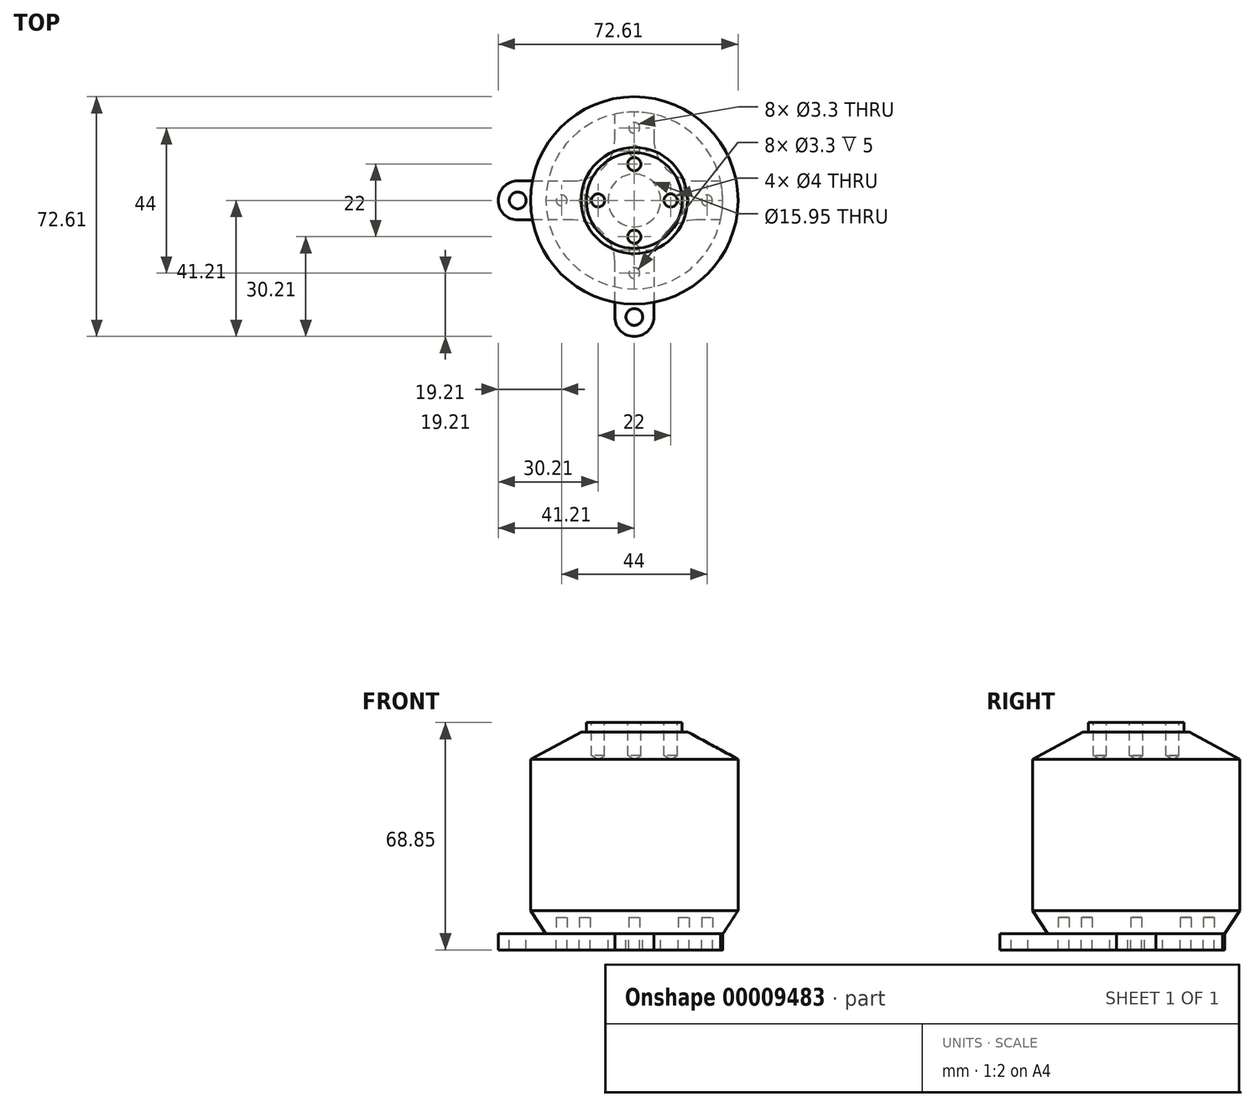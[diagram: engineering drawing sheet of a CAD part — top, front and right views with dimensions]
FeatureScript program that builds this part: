
annotation { "Feature Type Name" : "Feature", "Feature Type Description" : "" }
export const myFeature = defineFeature(function(context is Context, id is Id, definition is map)
    precondition{}
    {
        {
            var Q0;
            Q0=qCreatedBy(makeId("Front.planeOp"),FACE);
            var sketch = newSketch(context, id + "F0", { "sketchPlane" : qUnion([Q0])});
            skLineSegment(sketch, "E0", {"start": v(0, 0) * mm, "end": v(26.8, 0) * mm});
            skLineSegment(sketch, "E1", {"start": v(31.4, 7.03) * mm, "end": v(31.4, 52.91) * mm});
            skLineSegment(sketch, "E2", {"start": v(14.5, 64) * mm, "end": v(0, 64) * mm});
            skLineSegment(sketch, "E3", {"start": v(0, 64) * mm, "end": v(0, 0) * mm});
            skLineSegment(sketch, "E4.bottom", {"start": v(0, 0) * mm, "end": v(5, 0) * mm});
            skLineSegment(sketch, "E4.top", {"start": v(0, -24) * mm, "end": v(5, -24) * mm});
            skLineSegment(sketch, "E4.left", {"start": v(0, 0) * mm, "end": v(0, -24) * mm});
            skLineSegment(sketch, "E4.right", {"start": v(5, 0) * mm, "end": v(5, -24) * mm});
            skLineSegment(sketch, "E5", {"start": v(14.5, 64) * mm, "end": v(14.5, 61.2) * mm});
            skLineSegment(sketch, "E6", {"start": v(14.5, 61.2) * mm, "end": v(16.1, 61.2) * mm});
            skLineSegment(sketch, "E7", {"start": v(16.1, 61.2) * mm, "end": v(31.4, 52.91) * mm});
            skLineSegment(sketch, "E8", {"start": v(31.4, 7.03) * mm, "end": v(26.8, 0) * mm});
            skSolve(sketch);
        }
        {
            var Q0;
            Q0=makeQuery(id+"F0.imprint","IMPRINT",FACE,{"disambiguationData":[TD([[makeQuery(id+"F0.imprint","IMPRINT",EDGE,{"derivedFrom":sQuery(id+"F0.wireOp",EDGE,"E0")}),1.0]])]});
            var Q1;
            Q1=makeQuery(id+"F0.imprint","IMPRINT",FACE,{"disambiguationData":[TD([[makeQuery(id+"F0.imprint","IMPRINT",EDGE,{"derivedFrom":sQuery(id+"F0.wireOp",EDGE,"E4.bottom")}),-1.0]])]});
            var Q2;
            Q2=sQuery(id+"F0.wireOp",EDGE,"E3");
            revolve(context, id + "F1", {"entities" : qUnion([Q0, Q1]), "axis" : qUnion([Q2]), "revolveType" : RevolveType.FULL});
        }
        {
            var Q0;
            Q0=makeQuery(id+"F1.opRevolve","SWEPT_FACE",FACE,{"disambiguationData":[OSD([sQuery(id+"F0.wireOp",EDGE,"E0")])]});
            var sketch = newSketch(context, id + "F2", { "sketchPlane" : qUnion([Q0])});
            skCircle(sketch, "E9", {"center": v(-22, 0) * mm, "radius": 1.65 * mm});
            skCircle(sketch, "E10", {"center": v(-15, 0) * mm, "radius": 1.65 * mm});
            skCircle(sketch, "E11.1.0", {"center": v(0, -22) * mm, "radius": 1.65 * mm});
            skCircle(sketch, "E11.1.1", {"center": v(0, -15) * mm, "radius": 1.65 * mm});
            skCircle(sketch, "E11.2.0", {"center": v(22, 0) * mm, "radius": 1.65 * mm});
            skCircle(sketch, "E11.2.1", {"center": v(15, 0) * mm, "radius": 1.65 * mm});
            skCircle(sketch, "E11.3.0", {"center": v(0, 22) * mm, "radius": 1.65 * mm});
            skCircle(sketch, "E11.3.1", {"center": v(0, 15) * mm, "radius": 1.65 * mm});
            skPoint(sketch, "E11.center", {"position": v(0, 0) * mm});
            skSolve(sketch);
        }
        {
            var Q0;
            Q0=makeQuery(id+"F2.imprint","IMPRINT",FACE,{"disambiguationData":[TD([[makeQuery(id+"F2.imprint","IMPRINT",EDGE,{"derivedFrom":sQuery(id+"F2.wireOp",EDGE,"E9")}),1.0]])]});
            var Q1;
            Q1=makeQuery(id+"F2.imprint","IMPRINT",FACE,{"disambiguationData":[TD([[makeQuery(id+"F2.imprint","IMPRINT",EDGE,{"derivedFrom":sQuery(id+"F2.wireOp",EDGE,"E10")}),1.0]])]});
            var Q2;
            Q2=makeQuery(id+"F2.imprint","IMPRINT",FACE,{"disambiguationData":[TD([[makeQuery(id+"F2.imprint","IMPRINT",EDGE,{"derivedFrom":sQuery(id+"F2.wireOp",EDGE,"E11.3.1")}),1.0]])]});
            var Q3;
            Q3=makeQuery(id+"F2.imprint","IMPRINT",FACE,{"disambiguationData":[TD([[makeQuery(id+"F2.imprint","IMPRINT",EDGE,{"derivedFrom":sQuery(id+"F2.wireOp",EDGE,"E11.3.0")}),1.0]])]});
            var Q4;
            Q4=makeQuery(id+"F2.imprint","IMPRINT",FACE,{"disambiguationData":[TD([[makeQuery(id+"F2.imprint","IMPRINT",EDGE,{"derivedFrom":sQuery(id+"F2.wireOp",EDGE,"E11.2.1")}),1.0]])]});
            var Q5;
            Q5=makeQuery(id+"F2.imprint","IMPRINT",FACE,{"disambiguationData":[TD([[makeQuery(id+"F2.imprint","IMPRINT",EDGE,{"derivedFrom":sQuery(id+"F2.wireOp",EDGE,"E11.2.0")}),1.0]])]});
            var Q6;
            Q6=makeQuery(id+"F2.imprint","IMPRINT",FACE,{"disambiguationData":[TD([[makeQuery(id+"F2.imprint","IMPRINT",EDGE,{"derivedFrom":sQuery(id+"F2.wireOp",EDGE,"E11.1.1")}),1.0]])]});
            var Q7;
            Q7=makeQuery(id+"F2.imprint","IMPRINT",FACE,{"disambiguationData":[TD([[makeQuery(id+"F2.imprint","IMPRINT",EDGE,{"derivedFrom":sQuery(id+"F2.wireOp",EDGE,"E11.1.0")}),1.0]])]});
            extrude(context, id + "F3", {"entities" : qUnion([Q0, Q1, Q2, Q3, Q4, Q5, Q6, Q7]), "operationType" : NewBodyOperationType.REMOVE, "oppositeDirection" : true, "depth" : 5 * mm});
        }
        {
            var Q0;
            Q0=makeQuery(id+"F1.opRevolve","SWEPT_FACE",FACE,{"disambiguationData":[OSD([sQuery(id+"F0.wireOp",EDGE,"E0")])]});
            var sketch = newSketch(context, id + "F4", { "sketchPlane" : qUnion([Q0])});
            skLineSegment(sketch, "E12", {"start": v(-5.92, 35.3) * mm, "end": v(-5.92, 18.62) * mm});
            skLineSegment(sketch, "E13", {"start": v(-18.62, 5.92) * mm, "end": v(-35.3, 5.92) * mm});
            skLineSegment(sketch, "E14", {"start": v(-35.3, -5.92) * mm, "end": v(-18.62, -5.92) * mm});
            skLineSegment(sketch, "E15", {"start": v(-5.92, -18.62) * mm, "end": v(-5.92, -35.3) * mm});
            skLineSegment(sketch, "E16", {"start": v(5.92, -35.3) * mm, "end": v(5.92, -18.62) * mm});
            skLineSegment(sketch, "E17", {"start": v(18.62, -5.92) * mm, "end": v(35.3, -5.92) * mm});
            skLineSegment(sketch, "E18", {"start": v(35.3, 5.92) * mm, "end": v(18.62, 5.92) * mm});
            skLineSegment(sketch, "E19", {"start": v(5.92, 18.62) * mm, "end": v(5.92, 35.3) * mm});
            skArc(sketch, "E20", {"start": v(5.92, 35.3) * mm, "mid": v(0, 41.21) * mm, "end": v(-5.92, 35.3) * mm});
            skArc(sketch, "E21", {"start": v(5.92, -35.3) * mm, "mid": v(0, -41.21) * mm, "end": v(-5.92, -35.3) * mm});
            skArc(sketch, "E22", {"start": v(-35.3, 5.92) * mm, "mid": v(-41.21, 0) * mm, "end": v(-35.3, -5.92) * mm});
            skPoint(sketch, "E23.visualSharp", {"position": v(-5.92, 5.92) * mm});
            skArc(sketch, "E23.filletArc", {"start": v(-18.62, 5.92) * mm, "mid": v(-9.64, 9.64) * mm, "end": v(-5.92, 18.62) * mm});
            skPoint(sketch, "E24.visualSharp", {"position": v(5.92, 5.92) * mm});
            skArc(sketch, "E24.filletArc", {"start": v(5.92, 18.62) * mm, "mid": v(9.64, 9.64) * mm, "end": v(18.62, 5.92) * mm});
            skPoint(sketch, "E25.visualSharp", {"position": v(5.92, -5.92) * mm});
            skArc(sketch, "E25.filletArc", {"start": v(18.62, -5.92) * mm, "mid": v(9.64, -9.64) * mm, "end": v(5.92, -18.62) * mm});
            skPoint(sketch, "E26.visualSharp", {"position": v(-5.92, -5.92) * mm});
            skArc(sketch, "E26.filletArc", {"start": v(-5.92, -18.62) * mm, "mid": v(-9.64, -9.64) * mm, "end": v(-18.62, -5.92) * mm});
            skArc(sketch, "E27", {"start": v(35.3, 5.92) * mm, "mid": v(41.21, 0) * mm, "end": v(35.3, -5.92) * mm});
            skLineSegment(sketch, "E28", {"start": v(35.3, 5.92) * mm, "end": v(35.3, -5.92) * mm, "construction": true});
            skCircle(sketch, "E29", {"center": v(-35.3, 0) * mm, "radius": 2.54 * mm});
            skCircle(sketch, "E30", {"center": v(0, 35.3) * mm, "radius": 2.54 * mm});
            skCircle(sketch, "E31", {"center": v(35.3, 0) * mm, "radius": 2.54 * mm});
            skCircle(sketch, "E32", {"center": v(0, -35.3) * mm, "radius": 2.54 * mm});
            skCircle(sketch, "E33", {"center": v(0, 0) * mm, "radius": 7.98 * mm});
            skSolve(sketch);
        }
        {
            var Q0;
            {var subQ6=sQuery(id+"F4.wireOp",EDGE,"E22");Q0=makeQuery(id+"F4.imprint","IMPRINT",FACE,{"disambiguationData":[TD([[makeQuery(id+"F4.imprint","IMPRINT",EDGE,{"derivedFrom":subQ6}),1.0]])]});}
            var Q1;
            {var subQ12=sQuery(id+"F4.wireOp",EDGE,"E23.filletArc");Q1=makeQuery(id+"F4.imprint","IMPRINT",FACE,{"disambiguationData":[TD([[makeQuery(id+"F4.imprint","IMPRINT",EDGE,{"derivedFrom":subQ12}),-1.0]])]});}
            var Q2;
            {var subQ6=sQuery(id+"F4.wireOp",EDGE,"E27");Q2=makeQuery(id+"F4.imprint","IMPRINT",FACE,{"disambiguationData":[TD([[makeQuery(id+"F4.imprint","IMPRINT",EDGE,{"derivedFrom":subQ6}),-1.0]])]});}
            var Q3;
            {var subQ6=sQuery(id+"F4.wireOp",EDGE,"E21");Q3=makeQuery(id+"F4.imprint","IMPRINT",FACE,{"disambiguationData":[TD([[makeQuery(id+"F4.imprint","IMPRINT",EDGE,{"derivedFrom":subQ6}),-1.0]])]});}
            var Q4;
            {var subQ6=sQuery(id+"F4.wireOp",EDGE,"E20");Q4=makeQuery(id+"F4.imprint","IMPRINT",FACE,{"disambiguationData":[TD([[makeQuery(id+"F4.imprint","IMPRINT",EDGE,{"derivedFrom":subQ6}),1.0]])]});}
            extrude(context, id + "F5", {"entities" : qUnion([Q0, Q1, Q2, Q3, Q4]), "depth" : 4.85 * mm});
        }
        {
            var Q0;
            Q0=makeQuery(id+"F1.opRevolve","SWEPT_FACE",FACE,{"disambiguationData":[OSD([sQuery(id+"F0.wireOp",EDGE,"E2")])]});
            var sketch = newSketch(context, id + "F6", { "sketchPlane" : qUnion([Q0])});
            skLineSegment(sketch, "E34", {"start": v(0, 0) * mm, "end": v(-11, 0) * mm, "construction": true});
            skCircle(sketch, "E35", {"center": v(-11, 0) * mm, "radius": 2 * mm});
            skCircle(sketch, "E36.1.0", {"center": v(0, 11) * mm, "radius": 2 * mm});
            skCircle(sketch, "E36.2.0", {"center": v(11, 0) * mm, "radius": 2 * mm});
            skCircle(sketch, "E36.3.0", {"center": v(0, -11) * mm, "radius": 2 * mm});
            skPoint(sketch, "E36.center", {"position": v(0, 0) * mm});
            skLineSegment(sketch, "E36.anchor2", {"start": v(0, 0) * mm, "end": v(0, -11) * mm, "construction": true});
            skSolve(sketch);
        }
        {
            var Q0;
            Q0=sQuery(id+"F6.wireOp",VERTEX,"E34.end");
            var Q1;
            Q1=sQuery(id+"F6.wireOp",VERTEX,"E36.1.0.center");
            var Q2;
            Q2=sQuery(id+"F6.wireOp",VERTEX,"E36.2.0.center");
            var Q3;
            Q3=sQuery(id+"F6.wireOp",VERTEX,"E36.3.0.center");
            var Q4;
            Q4=makeQuery(id+"F1.opRevolve","SWEPT_BODY",BODY,{"disambiguationData":[OSD([sQuery(id+"F0.wireOp",EDGE,"E0"),sQuery(id+"F0.wireOp",EDGE,"E1"),sQuery(id+"F0.wireOp",EDGE,"E2"),sQuery(id+"F0.wireOp",EDGE,"E3"),sQuery(id+"F0.wireOp",EDGE,"E4.top"),sQuery(id+"F0.wireOp",EDGE,"E4.left"),sQuery(id+"F0.wireOp",EDGE,"E4.right"),sQuery(id+"F0.wireOp",EDGE,"E5"),sQuery(id+"F0.wireOp",EDGE,"E6"),sQuery(id+"F0.wireOp",EDGE,"E7"),sQuery(id+"F0.wireOp",EDGE,"E8")])]});
            hole(context, id + "F7", {"style" : HoleStyle.SIMPLE, "holeDiameter" : 4 * mm, "endStyle" : HoleEndStyle.BLIND, "holeDepth" : 10 * mm, "locations" : qUnion([Q0, Q1, Q2, Q3]), "scope" : qUnion([Q4])});
        }
    });
